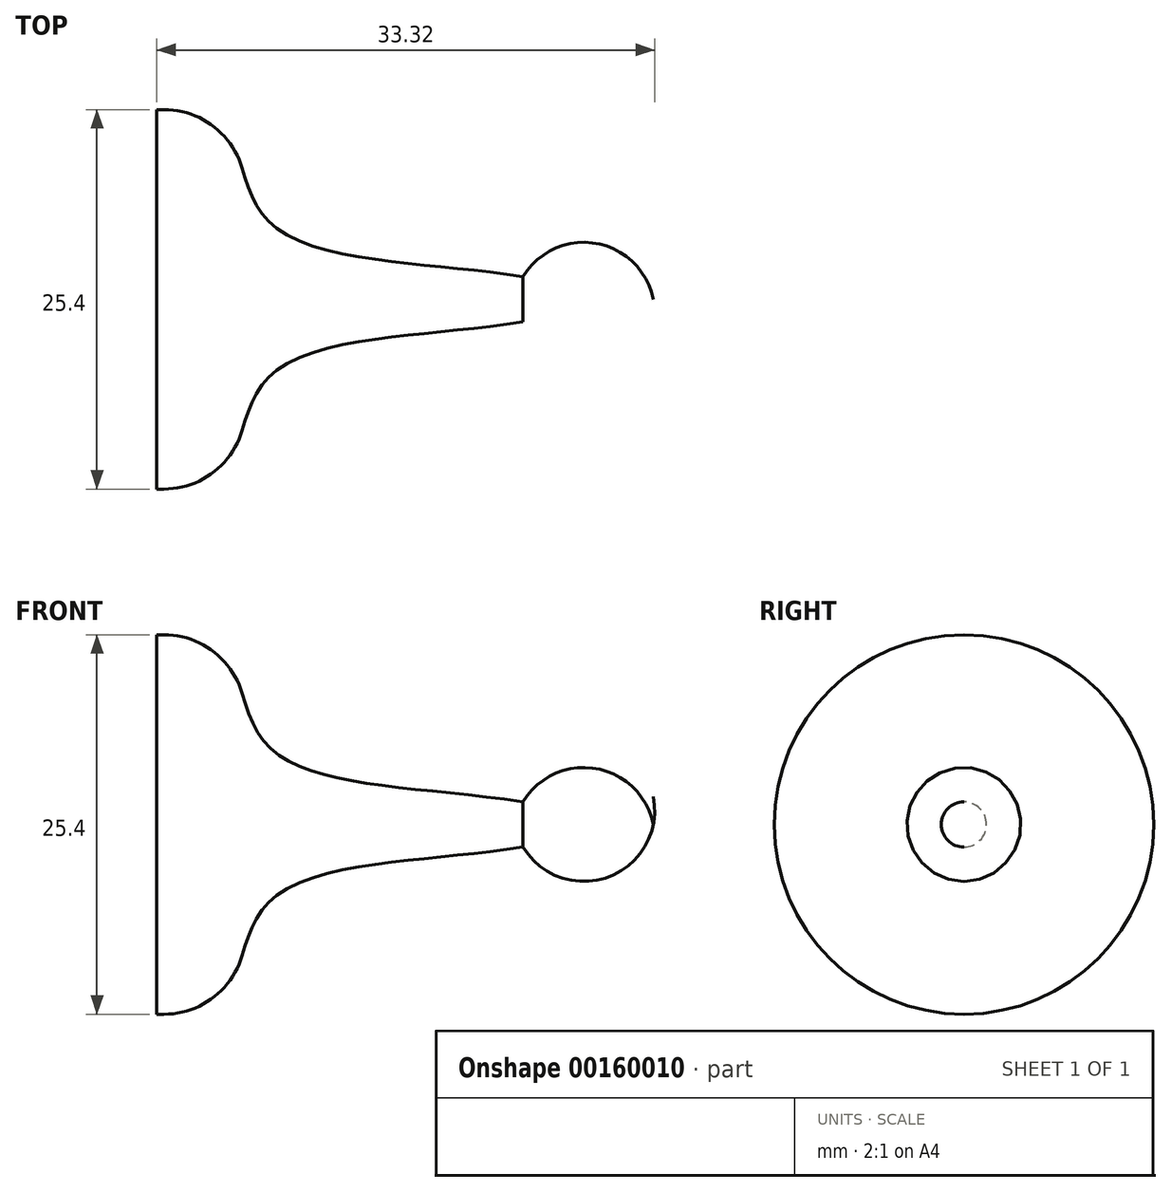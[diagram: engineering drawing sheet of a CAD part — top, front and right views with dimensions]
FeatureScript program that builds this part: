
annotation { "Feature Type Name" : "Feature", "Feature Type Description" : "" }
export const myFeature = defineFeature(function(context is Context, id is Id, definition is map)
    precondition{}
    {
        {
            var Q0;
            Q0=qCreatedBy(makeId("Front.planeOp"),FACE);
            var sketch = newSketch(context, id + "F0", { "sketchPlane" : qUnion([Q0])});
            skLineSegment(sketch, "E0", {"start": v(0, 12.7) * mm, "end": v(0.48, 12.7) * mm});
            skArc(sketch, "E1", {"start": v(33.23, 0) * mm, "mid": v(29.39, 3.74) * mm, "end": v(24.5, 1.52) * mm});
            skFitSpline(sketch, "E2", {"points": [v(4.07, 12.7) * mm, v(7.32, 5.4) * mm, v(24.5, 1.52) * mm], "startDerivative": vector(11.74, -13.01) * mm, "endDerivative": vector(36.37, -5.51) * mm});
            skArc(sketch, "E3.filletArc", {"start": v(5.7, 8.78) * mm, "mid": v(3.75, 11.61) * mm, "end": v(0.48, 12.7) * mm});
            skPoint(sketch, "E4.start.orphan", {"position": v(-64.76, 0) * mm});
            skLineSegment(sketch, "E5", {"start": v(0, 12.7) * mm, "end": v(0, 0) * mm});
            skLineSegment(sketch, "E6", {"start": v(0, 0) * mm, "end": v(33.23, 0) * mm});
            skSolve(sketch);
        }
        {
            var Q0;
            Q0=makeQuery(id+"F0.imprint","IMPRINT",FACE,{"disambiguationData":[TD([[makeQuery(id+"F0.imprint","IMPRINT",EDGE,{"derivedFrom":sQuery(id+"F0.wireOp",EDGE,"E0")}),-1.0]])]});
            var Q1;
            Q1=sQuery(id+"F0.wireOp",EDGE,"E6");
            revolve(context, id + "F1", {"entities" : qUnion([Q0]), "axis" : qUnion([Q1]), "revolveType" : RevolveType.ONE_DIRECTION, "angle" : 360 * degree});
        }
    });
